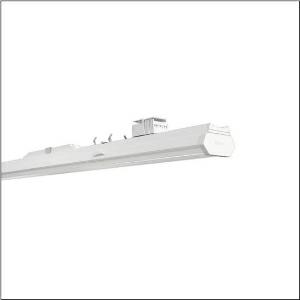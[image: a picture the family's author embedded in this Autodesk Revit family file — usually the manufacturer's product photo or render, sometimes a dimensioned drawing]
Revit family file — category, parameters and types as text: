
# Revit family: licross_r__11_protected_tw_51ts12tnt75w_3e19
name_source: partatom
category: Lighting Fixtures
units: mm (PartAtom-declared; Revit-internal decimal feet)

## family parameters
Cut with Voids When Loaded = No
Host = Face
Light Source = No
Part Type = Normal
Room Calculation Point = No
Round Connector Dimension = Use Diameter
Shared = No

## types (1)
- --- (1 x LED 2700 K ... 6500 K, 7740 lm, 57.4 W, 2700K)
    Apparent Load = 57 VA
    CIE Flux Codes = 54 82 95 97 100
    Color Rendering = 80
    Color Temperature = 2700K
    Default Elevation = 1800 mm
    Description = Licross® 11 Protected TWluminaire insert, length: 1.500mm, width: 90mm, height: 101mm, LED rated luminous flux: 7.740lm, light colour: 8tw, control gear: DALI DT8, control gear: ECG DALI, with plug, 5-pole, with phase selection, mains connection: 220..240V, AC, 50/60Hz, halogen-free wiring, primary optical cover: cover, of PMMA, light emission: direct with ceiling illumination distribution, protection rating (complete): IP50, insulation class (complete): insulation class I (protective earthing), certification: CE, ENEC, VDE, protection symbol: D if used in an environment with non-conductive dust loads with corresponding accessories, permissible ambient temperature for indoor applications: -25..+40°C, reducing of maximum allowable ambient temperature of 5°C with ceiling mounting, corresponds to IFS (International Featured Standards) requirements for safety and quality in the food industry, packaging unit: 1 piece
    Height = 92 mm
    Lamp = 1 x LED 2700 K ... 6500 K
    Lamp Light Flux = 7740 lm
    Lamp Power = 57.4 W
    Lamp count = 1
    Length = 1500 mm
    Luminous efficacy = 135 lm/W
    Manufacturer = Siteco
    ModVariant = No
    Model = 51TS12TNT75W
    Mounting Place = Ceiling
    Mounting Type = Pendant
    Number of Poles = 1
    OnlyDefault = Yes
    Power Factor = 1
    Product Name = Licross® 11 Protected TW
    Product group = luminaire insert
    ProductGroupID = 902
    Protection Class = Protection class I
    Protection Degree = IP 50
    RLX_Detail_Level = 1
    RlxData = <blob elided: 20373 chars, md5=549d367f>
    Socket = socket
    Standby Power = 0 W
    System Light Flux = 7740 lm
    System Power = 57 W
    Type Comments = individual setting: CCT=2700K
    Type Image = l_1256145.jpg
    URL = http://relux.com
    VarID = @adj_138203
    Voltage = 0 V
    Weight = 0.00 kg
    Width = 88 mm

## geometry (parser evidence)
native form markers: Blend x4, Sweep x12
no freeform markers — native parametric forms only
